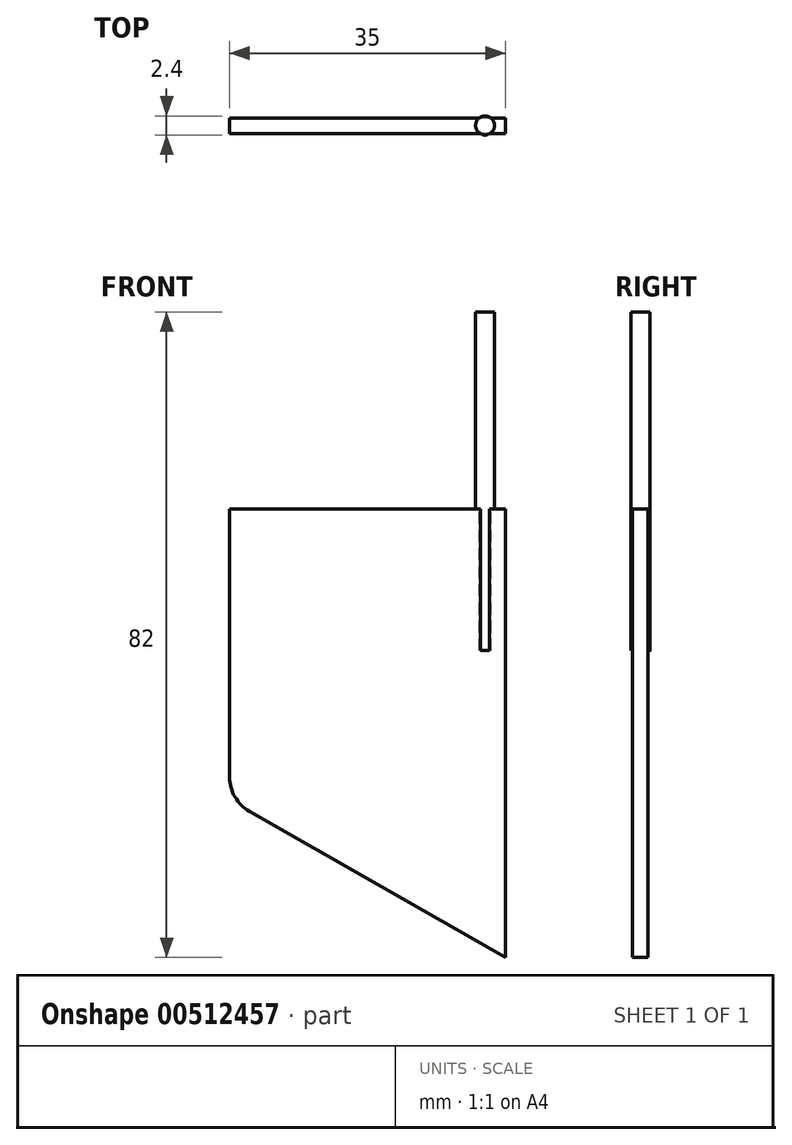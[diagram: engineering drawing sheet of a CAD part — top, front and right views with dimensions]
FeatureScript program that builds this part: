
annotation { "Feature Type Name" : "Feature", "Feature Type Description" : "" }
export const myFeature = defineFeature(function(context is Context, id is Id, definition is map)
    precondition{}
    {
        {
            var Q0;
            Q0=qCreatedBy(makeId("Front.planeOp"),FACE);
            var sketch = newSketch(context, id + "F0", { "sketchPlane" : qUnion([Q0])});
            skLineSegment(sketch, "E0", {"start": v(0, 30.66) * mm, "end": v(0, -26.34) * mm});
            skLineSegment(sketch, "E1", {"start": v(0, 30.66) * mm, "end": v(-35, 30.66) * mm});
            skLineSegment(sketch, "E2", {"start": v(-35, 30.66) * mm, "end": v(-35, -6.34) * mm});
            skLineSegment(sketch, "E3", {"start": v(-35, -6.34) * mm, "end": v(0, -26.34) * mm});
            skSolve(sketch);
        }
        {
            var Q0;
            Q0=makeQuery(id+"F0.imprint","IMPRINT",FACE,{"disambiguationData":[TD([[makeQuery(id+"F0.imprint","IMPRINT",EDGE,{"derivedFrom":sQuery(id+"F0.wireOp",EDGE,"E0")}),-1.0]])]});
            extrude(context, id + "F1", {"entities" : qUnion([Q0]), "depth" : 2 * mm});
        }
        {
            var Q0;
            Q0=makeQuery(id+"F1.opExtrude","SWEPT_FACE",FACE,{"disambiguationData":[OSD([sQuery(id+"F0.wireOp",EDGE,"E1")])]});
            var sketch = newSketch(context, id + "F2", { "sketchPlane" : qUnion([Q0])});
            skCircle(sketch, "E4", {"center": v(-2.56, -0.95) * mm, "radius": 1.2 * mm});
            skSolve(sketch);
        }
        {
            var Q0;
            {var subQ0=sQuery(id+"F2.wireOp",EDGE,"E4");var subQ1=makeQuery(id+"F1.opExtrude","CAP_EDGE",EDGE,{"disambiguationData":[OSD([sQuery(id+"F0.wireOp",EDGE,"E1")])],"isStart":true});var subQ2=makeQuery(id+"F2.imprint","INTERSECT",VERTEX,{"disambiguationData":[OD(0.0)],"derivedFrom":[subQ1,subQ0]});Q0=makeQuery(id+"F2.imprint","IMPRINT",FACE,{"disambiguationData":[TD([[makeQuery(id+"F2.imprint","IMPRINT",EDGE,{"disambiguationData":[TD([[subQ2,1.0]])],"derivedFrom":subQ0}),1.0]])]});}
            var Q1;
            {var subQ0=sQuery(id+"F2.wireOp",EDGE,"E4");var subQ1=makeQuery(id+"F1.opExtrude","CAP_EDGE",EDGE,{"disambiguationData":[OSD([sQuery(id+"F0.wireOp",EDGE,"E1")])],"isStart":false});var subQ2=makeQuery(id+"F2.imprint","INTERSECT",VERTEX,{"disambiguationData":[OD(0.0)],"derivedFrom":[subQ1,subQ0]});Q1=makeQuery(id+"F2.imprint","IMPRINT",FACE,{"disambiguationData":[TD([[makeQuery(id+"F2.imprint","IMPRINT",EDGE,{"disambiguationData":[TD([[subQ2,-1.0]])],"derivedFrom":subQ0}),1.0]])]});}
            extrude(context, id + "F3", {"entities" : qUnion([Q0, Q1]), "operationType" : NewBodyOperationType.ADD, "oppositeDirection" : true, "depth" : 18 * mm});
        }
        {
            var Q0;
            {var subQ0=sQuery(id+"F2.wireOp",EDGE,"E4");var subQ1=sQuery(id+"F0.wireOp",EDGE,"E1");var subQ2=makeQuery(id+"F1.opExtrude","CAP_EDGE",EDGE,{"disambiguationData":[OSD([subQ1])],"isStart":true});var subQ3=makeQuery(id+"F2.imprint","INTERSECT",VERTEX,{"disambiguationData":[OD(0.0)],"derivedFrom":[subQ2,subQ0]});Q0=makeQuery(id+"F2.imprint","IMPRINT",FACE,{"disambiguationData":[TD([[makeQuery(id+"F2.imprint","IMPRINT",EDGE,{"disambiguationData":[TD([[subQ3,-1.0]])],"derivedFrom":subQ0}),1.0]])]});}
            extrude(context, id + "F4", {"entities" : qUnion([Q0]), "operationType" : NewBodyOperationType.ADD, "depth" : 25 * mm});
        }
        {
            var Q0;
            {var subQ0=sQuery(id+"F2.wireOp",EDGE,"E4");var subQ1=makeQuery(id+"F1.opExtrude","CAP_EDGE",EDGE,{"disambiguationData":[OSD([sQuery(id+"F0.wireOp",EDGE,"E1")])],"isStart":false});var subQ2=makeQuery(id+"F2.imprint","INTERSECT",VERTEX,{"disambiguationData":[OD(0.0)],"derivedFrom":[subQ1,subQ0]});Q0=makeQuery(id+"F2.imprint","IMPRINT",FACE,{"disambiguationData":[TD([[makeQuery(id+"F2.imprint","IMPRINT",EDGE,{"disambiguationData":[TD([[subQ2,-1.0]])],"derivedFrom":subQ0}),1.0]])]});}
            var Q1;
            {var subQ0=sQuery(id+"F2.wireOp",EDGE,"E4");var subQ1=makeQuery(id+"F1.opExtrude","CAP_EDGE",EDGE,{"disambiguationData":[OSD([sQuery(id+"F0.wireOp",EDGE,"E1")])],"isStart":true});var subQ2=makeQuery(id+"F2.imprint","INTERSECT",VERTEX,{"disambiguationData":[OD(0.0)],"derivedFrom":[subQ1,subQ0]});Q1=makeQuery(id+"F2.imprint","IMPRINT",FACE,{"disambiguationData":[TD([[makeQuery(id+"F2.imprint","IMPRINT",EDGE,{"disambiguationData":[TD([[subQ2,1.0]])],"derivedFrom":subQ0}),1.0]])]});}
            extrude(context, id + "F5", {"entities" : qUnion([Q0, Q1]), "operationType" : NewBodyOperationType.ADD, "depth" : 25 * mm});
        }
        {
            var Q0;
            Q0=makeQuery(id+"F1.opExtrude","SWEPT_EDGE",EDGE,{"disambiguationData":[OSD([sQuery(id+"F0.wireOp",EDGE,"E2"),sQuery(id+"F0.wireOp",EDGE,"E3")])]});
            fillet(context, id + "F6", {"entities" : qUnion([Q0]), "radius" : 5 * mm, "tangentPropagation" : true, "allowEdgeOverflow" : false});
        }
    });
